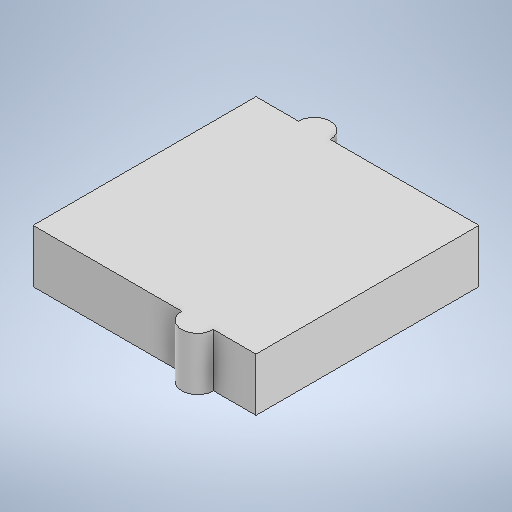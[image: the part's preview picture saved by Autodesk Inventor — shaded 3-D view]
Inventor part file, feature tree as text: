
AUTODESK INVENTOR PART (.ipt)
format: ipt  version: 2025.1 (Build 291241000, 241)  size: 222,720 bytes
history: native  units: mm
features: extrude x2, sketch x2
ambient origin geometry x8: Origin, YZ Plane, XZ Plane, XY Plane, X Axis, Y Axis, Z Axis, Center Point
bodies: Volumenkörper1 (feature_tree)
feature tree (4):
  extrude  "Extrusion1"  Depth=21.0mm
  extrude  "Extrusion2"  Depth=5.0mm
  sketch  "Skizze1"  dims[d0=21.0mm d1=21.0mm]
  sketch  "Skizze2"  dims[d2=5.0mm d3=0.0mm d4=3.0mm d5=3.0mm d6=5.0mm d7=5.0mm d8=5.0mm d9=0.0mm]
